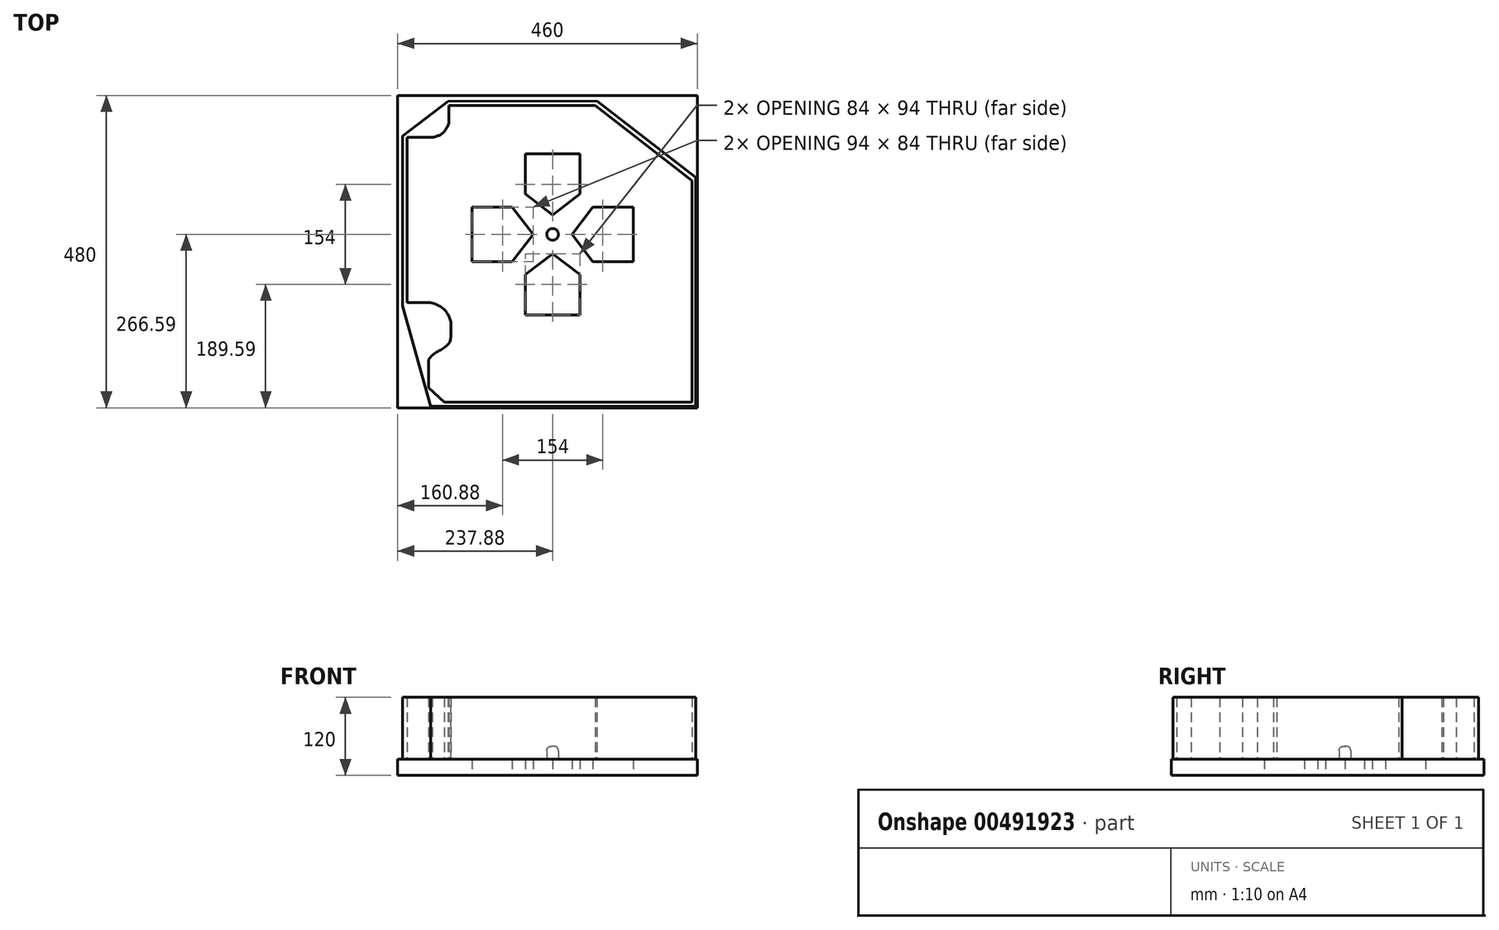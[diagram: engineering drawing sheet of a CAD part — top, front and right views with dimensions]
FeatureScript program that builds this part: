
annotation { "Feature Type Name" : "Feature", "Feature Type Description" : "" }
export const myFeature = defineFeature(function(context is Context, id is Id, definition is map)
    precondition{}
    {
        {
            var Q0;
            Q0=qCreatedBy(makeId("Top.planeOp"),FACE);
            var sketch = newSketch(context, id + "F0", { "sketchPlane" : qUnion([Q0])});
            skLineSegment(sketch, "E0.bottom", {"start": v(-237.88, 213.4) * mm, "end": v(222.12, 213.4) * mm});
            skLineSegment(sketch, "E0.top", {"start": v(-237.88, -266.6) * mm, "end": v(222.12, -266.6) * mm});
            skLineSegment(sketch, "E0.left", {"start": v(-237.88, 213.4) * mm, "end": v(-237.88, -266.6) * mm});
            skLineSegment(sketch, "E0.right", {"start": v(222.12, 213.4) * mm, "end": v(222.12, -266.6) * mm});
            skSolve(sketch);
        }
        {
            var Q0;
            Q0=makeQuery(id+"F0.imprint","IMPRINT",FACE,{"disambiguationData":[TD([[makeQuery(id+"F0.imprint","IMPRINT",EDGE,{"derivedFrom":sQuery(id+"F0.wireOp",EDGE,"E0.bottom")}),-1.0]])]});
            extrude(context, id + "F1", {"entities" : qUnion([Q0]), "depth" : 25 * mm});
        }
        {
            var Q0;
            Q0=qCreatedBy(makeId("Top.planeOp"),FACE);
            var sketch = newSketch(context, id + "F2", { "sketchPlane" : qUnion([Q0])});
            skLineSegment(sketch, "E1", {"start": v(-159.16, 198.28) * mm, "end": v(65.26, 198.28) * mm});
            skLineSegment(sketch, "E2", {"start": v(65.26, 198.28) * mm, "end": v(214.08, 82.44) * mm});
            skLineSegment(sketch, "E3", {"start": v(214.08, 82.44) * mm, "end": v(214.08, -258.18) * mm});
            skLineSegment(sketch, "E4", {"start": v(214.08, -258.18) * mm, "end": v(-166.07, -258.18) * mm});
            skLineSegment(sketch, "E5", {"start": v(-166.07, -258.18) * mm, "end": v(-190.4, -235.95) * mm});
            skLineSegment(sketch, "E6", {"start": v(-190.4, -235.95) * mm, "end": v(-190.4, -192.65) * mm});
            skLineSegment(sketch, "E7", {"start": v(-223.58, -105) * mm, "end": v(-223.58, 148.8) * mm});
            skLineSegment(sketch, "E8", {"start": v(-223.58, 148.8) * mm, "end": v(-184.87, 148.8) * mm});
            skLineSegment(sketch, "E9", {"start": v(-159.16, 198.28) * mm, "end": v(-159.16, 170.64) * mm});
            skFitSpline(sketch, "E10", {"points": [v(-184.87, 148.8) * mm, v(-159.16, 170.64) * mm], "startDerivative": vector(47.28, 10.78) * mm, "endDerivative": vector(18.25, 41.47) * mm});
            skLineSegment(sketch, "E11", {"start": v(-223.58, -105) * mm, "end": v(-187.64, -105) * mm});
            skLineSegment(sketch, "E12", {"start": v(-156.4, -134.32) * mm, "end": v(-156.4, -157.54) * mm});
            skFitSpline(sketch, "E13", {"points": [v(-156.4, -157.54) * mm, v(-190.4, -192.65) * mm], "startDerivative": vector(0.83, -56.4) * mm, "endDerivative": vector(-32.35, -49.77) * mm});
            skFitSpline(sketch, "E14", {"points": [v(-156.4, -134.32) * mm, v(-187.64, -105) * mm], "startDerivative": vector(-9.95, 40.64) * mm, "endDerivative": vector(-60.55, 12.44) * mm});
            skLineSegment(sketch, "E15", {"start": v(-160.82, 204.09) * mm, "end": v(-230.5, 151.28) * mm});
            skLineSegment(sketch, "E16", {"start": v(-230.5, 151.28) * mm, "end": v(-230.5, -109.7) * mm});
            skLineSegment(sketch, "E17", {"start": v(-230.5, -109.7) * mm, "end": v(-187.46, -264.26) * mm});
            skLineSegment(sketch, "E18", {"start": v(-187.46, -264.26) * mm, "end": v(219.88, -264.26) * mm});
            skLineSegment(sketch, "E19", {"start": v(219.88, -264.26) * mm, "end": v(219.88, 87.42) * mm});
            skLineSegment(sketch, "E20", {"start": v(219.88, 87.42) * mm, "end": v(67.82, 204.92) * mm});
            skLineSegment(sketch, "E21", {"start": v(67.82, 204.92) * mm, "end": v(-160.82, 204.09) * mm});
            skSolve(sketch);
        }
        {
            var Q0;
            Q0=qSketchRegion(id+"F2",true);
            extrude(context, id + "F3", {"entities" : qUnion([Q0]), "operationType" : NewBodyOperationType.ADD, "depth" : 120 * mm});
        }
        {
            var Q0;
            Q0=qCreatedBy(makeId("Top.planeOp"),FACE);
            var sketch = newSketch(context, id + "F4", { "sketchPlane" : qUnion([Q0])});
            skLineSegment(sketch, "E22", {"start": v(0, 171.16) * mm, "end": v(0, -195.2) * mm, "construction": true});
            skLineSegment(sketch, "E23", {"start": v(-192.62, 0) * mm, "end": v(196.95, 0) * mm, "construction": true});
            skLineSegment(sketch, "E24", {"start": v(-42, 124) * mm, "end": v(-42, 62) * mm});
            skLineSegment(sketch, "E25", {"start": v(-42, 62) * mm, "end": v(0, 30) * mm});
            skLineSegment(sketch, "E26", {"start": v(-42, 124) * mm, "end": v(0, 124) * mm});
            skLineSegment(sketch, "E27.MirrorCS", {"start": v(42, 124) * mm, "end": v(0, 124) * mm});
            skLineSegment(sketch, "E28.MirrorCS", {"start": v(42, 124) * mm, "end": v(42, 62) * mm});
            skLineSegment(sketch, "E29.MirrorCS", {"start": v(42, 62) * mm, "end": v(0, 30) * mm});
            skLineSegment(sketch, "E30.1.0", {"start": v(-124, -42) * mm, "end": v(-124, 0) * mm});
            skLineSegment(sketch, "E30.1.1", {"start": v(-124, 42) * mm, "end": v(-124, 0) * mm});
            skLineSegment(sketch, "E30.1.2", {"start": v(-124, 42) * mm, "end": v(-62, 42) * mm});
            skLineSegment(sketch, "E30.1.3", {"start": v(-62, 42) * mm, "end": v(-30, 0) * mm});
            skLineSegment(sketch, "E30.1.4", {"start": v(-62, -42) * mm, "end": v(-30, 0) * mm});
            skLineSegment(sketch, "E30.1.5", {"start": v(-124, -42) * mm, "end": v(-62, -42) * mm});
            skLineSegment(sketch, "E30.2.0", {"start": v(42, -124) * mm, "end": v(0, -124) * mm});
            skLineSegment(sketch, "E30.2.1", {"start": v(-42, -124) * mm, "end": v(0, -124) * mm});
            skLineSegment(sketch, "E30.2.2", {"start": v(-42, -124) * mm, "end": v(-42, -62) * mm});
            skLineSegment(sketch, "E30.2.3", {"start": v(-42, -62) * mm, "end": v(0, -30) * mm});
            skLineSegment(sketch, "E30.2.4", {"start": v(42, -62) * mm, "end": v(0, -30) * mm});
            skLineSegment(sketch, "E30.2.5", {"start": v(42, -124) * mm, "end": v(42, -62) * mm});
            skLineSegment(sketch, "E30.3.0", {"start": v(124, 42) * mm, "end": v(124, 0) * mm});
            skLineSegment(sketch, "E30.3.1", {"start": v(124, -42) * mm, "end": v(124, 0) * mm});
            skLineSegment(sketch, "E30.3.2", {"start": v(124, -42) * mm, "end": v(62, -42) * mm});
            skLineSegment(sketch, "E30.3.3", {"start": v(62, -42) * mm, "end": v(30, 0) * mm});
            skLineSegment(sketch, "E30.3.4", {"start": v(62, 42) * mm, "end": v(30, 0) * mm});
            skLineSegment(sketch, "E30.3.5", {"start": v(124, 42) * mm, "end": v(62, 42) * mm});
            skPoint(sketch, "E30.center", {"position": v(0, 0) * mm});
            skCircle(sketch, "E31", {"center": v(0, 0) * mm, "radius": 9 * mm});
            skSolve(sketch);
        }
        {
            var Q0;
            Q0=makeQuery(id+"F4.imprint","IMPRINT",FACE,{"disambiguationData":[TD([[makeQuery(id+"F4.imprint","IMPRINT",EDGE,{"derivedFrom":sQuery(id+"F4.wireOp",EDGE,"E24")}),1.0]])]});
            var Q1;
            Q1=makeQuery(id+"F4.imprint","IMPRINT",FACE,{"disambiguationData":[TD([[makeQuery(id+"F4.imprint","IMPRINT",EDGE,{"derivedFrom":sQuery(id+"F4.wireOp",EDGE,"E30.3.0")}),-1.0]])]});
            var Q2;
            Q2=makeQuery(id+"F4.imprint","IMPRINT",FACE,{"disambiguationData":[TD([[makeQuery(id+"F4.imprint","IMPRINT",EDGE,{"derivedFrom":sQuery(id+"F4.wireOp",EDGE,"E30.1.0")}),-1.0]])]});
            var Q3;
            Q3=makeQuery(id+"F4.imprint","IMPRINT",FACE,{"disambiguationData":[TD([[makeQuery(id+"F4.imprint","IMPRINT",EDGE,{"derivedFrom":sQuery(id+"F4.wireOp",EDGE,"E30.2.0")}),-1.0]])]});
            extrude(context, id + "F5", {"entities" : qUnion([Q0, Q1, Q2, Q3]), "operationType" : NewBodyOperationType.REMOVE, "endBound" : BoundingType.UP_TO_NEXT, "depth" : 25 * mm});
        }
        {
            var Q0;
            Q0=makeQuery(id+"F4.imprint","IMPRINT",FACE,{"disambiguationData":[TD([[makeQuery(id+"F4.imprint","IMPRINT",EDGE,{"derivedFrom":sQuery(id+"F4.wireOp",EDGE,"E31")}),1.0]])]});
            extrude(context, id + "F6", {"entities" : qUnion([Q0]), "operationType" : NewBodyOperationType.ADD, "depth" : 45 * mm});
        }
        {
            var Q0;
            Q0=makeQuery(id+"F6.opExtrude","CAP_EDGE",EDGE,{"disambiguationData":[OSD([sQuery(id+"F4.wireOp",EDGE,"E31")])],"isStart":false});
            fillet(context, id + "F7", {"entities" : qUnion([Q0]), "radius" : 7 * mm, "tangentPropagation" : true, "allowEdgeOverflow" : false});
        }
    });
